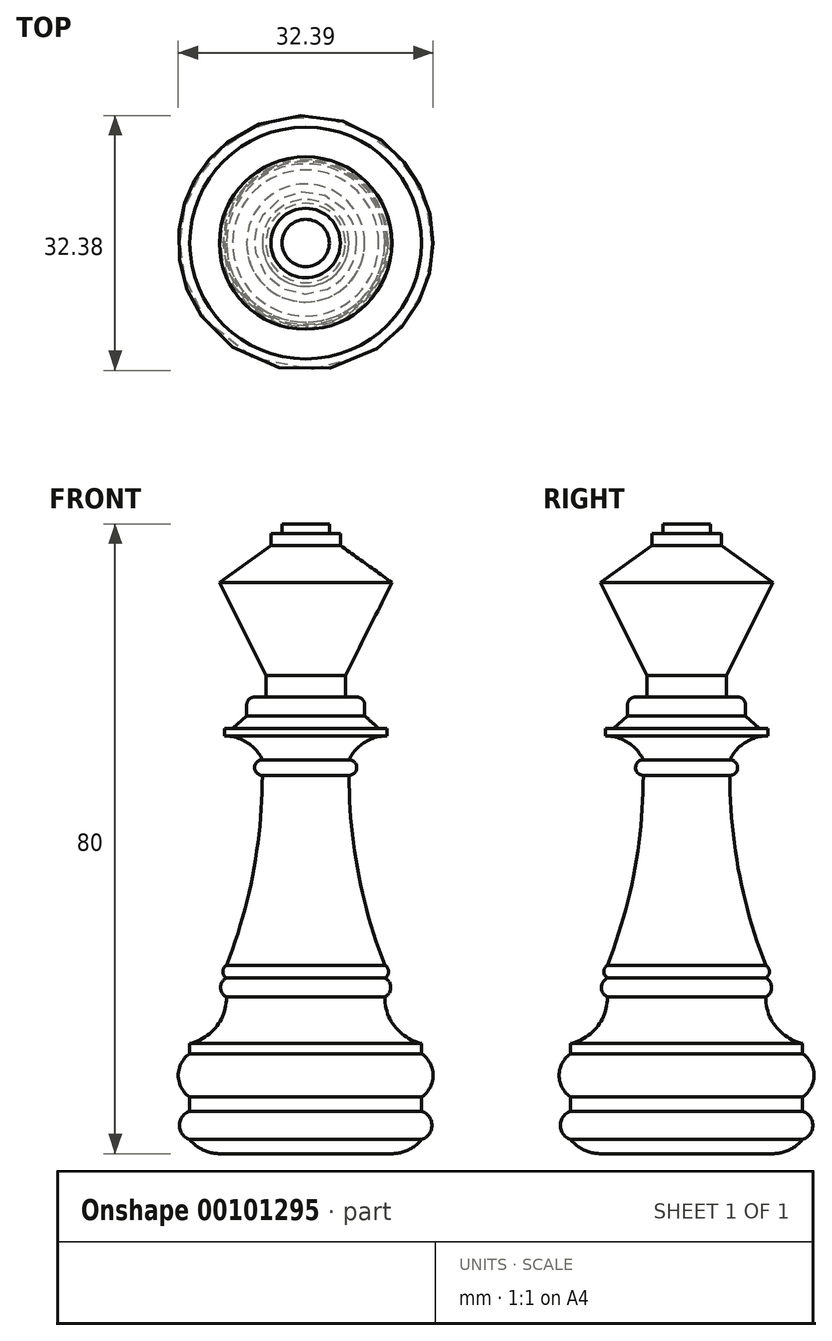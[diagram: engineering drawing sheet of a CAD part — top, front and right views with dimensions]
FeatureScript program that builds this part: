
annotation { "Feature Type Name" : "Feature", "Feature Type Description" : "" }
export const myFeature = defineFeature(function(context is Context, id is Id, definition is map)
    precondition{}
    {
        {
            var Q0;
            Q0=qCreatedBy(makeId("Front.planeOp"),FACE);
            var sketch = newSketch(context, id + "F0", { "sketchPlane" : qUnion([Q0])});
            skLineSegment(sketch, "E0", {"start": v(-203.37, 101.25) * mm, "end": v(-203.37, 21.25) * mm});
            skLineSegment(sketch, "E1", {"start": v(-203.37, 21.25) * mm, "end": v(-188.64, 21.25) * mm});
            skLineSegment(sketch, "E2", {"start": v(-188.64, 21.25) * mm, "end": v(-188.64, 23.04) * mm});
            skArc(sketch, "E3", {"start": v(-188.64, 23.04) * mm, "mid": v(-187.33, 24.85) * mm, "end": v(-188.64, 26.65) * mm});
            skLineSegment(sketch, "E4", {"start": v(-188.64, 26.65) * mm, "end": v(-188.64, 28.44) * mm});
            skArc(sketch, "E5", {"start": v(-188.64, 28.44) * mm, "mid": v(-187.17, 31.2) * mm, "end": v(-188.64, 33.94) * mm});
            skLineSegment(sketch, "E6", {"start": v(-188.64, 33.94) * mm, "end": v(-188.64, 35.24) * mm});
            skLineSegment(sketch, "E7", {"start": v(-188.64, 35.24) * mm, "end": v(-193.3, 35.24) * mm});
            skLineSegment(sketch, "E8", {"start": v(-193.3, 35.24) * mm, "end": v(-193.3, 41.17) * mm});
            skArc(sketch, "E9", {"start": v(-193.3, 41.17) * mm, "mid": v(-192.56, 42.37) * mm, "end": v(-193.3, 43.57) * mm});
            skArc(sketch, "E10", {"start": v(-193.3, 43.57) * mm, "mid": v(-192.84, 44.37) * mm, "end": v(-193.3, 45.17) * mm});
            skLineSegment(sketch, "E11", {"start": v(-197.86, 69.31) * mm, "end": v(-197.86, 45.17) * mm});
            skLineSegment(sketch, "E12", {"start": v(-197.86, 45.17) * mm, "end": v(-193.3, 45.17) * mm});
            skArc(sketch, "E13", {"start": v(-197.86, 69.31) * mm, "mid": v(-196.88, 70.3) * mm, "end": v(-197.86, 71.28) * mm});
            skLineSegment(sketch, "E14", {"start": v(-197.86, 71.28) * mm, "end": v(-197.86, 74.33) * mm});
            skLineSegment(sketch, "E15", {"start": v(-197.86, 74.33) * mm, "end": v(-193.04, 74.33) * mm});
            skLineSegment(sketch, "E16", {"start": v(-193.04, 74.33) * mm, "end": v(-193.04, 75.27) * mm});
            skLineSegment(sketch, "E17", {"start": v(-193.04, 75.27) * mm, "end": v(-194.08, 75.27) * mm});
            skLineSegment(sketch, "E18", {"start": v(-194.08, 75.27) * mm, "end": v(-195.87, 76.85) * mm});
            skLineSegment(sketch, "E19", {"start": v(-195.87, 76.85) * mm, "end": v(-195.87, 79.26) * mm});
            skLineSegment(sketch, "E20", {"start": v(-195.87, 79.26) * mm, "end": v(-198.32, 79.26) * mm});
            skArc(sketch, "E21", {"start": v(-198.32, 79.26) * mm, "mid": v(-197.8, 79.94) * mm, "end": v(-198.32, 80.62) * mm});
            skLineSegment(sketch, "E22", {"start": v(-198.32, 81.98) * mm, "end": v(-192.4, 93.8) * mm});
            skLineSegment(sketch, "E23", {"start": v(-192.4, 93.8) * mm, "end": v(-198.95, 98.5) * mm});
            skLineSegment(sketch, "E24", {"start": v(-198.95, 98.5) * mm, "end": v(-198.95, 100.03) * mm});
            skLineSegment(sketch, "E25", {"start": v(-198.95, 100.03) * mm, "end": v(-200.37, 100.03) * mm});
            skLineSegment(sketch, "E26", {"start": v(-200.37, 100.03) * mm, "end": v(-200.37, 101.25) * mm});
            skLineSegment(sketch, "E27", {"start": v(-200.37, 101.25) * mm, "end": v(-203.37, 101.25) * mm});
            skArc(sketch, "E28", {"start": v(-198.32, 80.62) * mm, "mid": v(-197.8, 81.3) * mm, "end": v(-198.32, 81.98) * mm});
            skLineSegment(sketch, "E29", {"start": v(-198.32, 81.98) * mm, "end": v(-198.32, 80.62) * mm});
            skLineSegment(sketch, "E30", {"start": v(-198.32, 79.26) * mm, "end": v(-198.32, 80.62) * mm});
            skSolve(sketch);
        }
        {
            var Q0;
            Q0=makeQuery(id+"F0.imprint","IMPRINT",FACE,{"disambiguationData":[TD([[makeQuery(id+"F0.imprint","IMPRINT",EDGE,{"derivedFrom":sQuery(id+"F0.wireOp",EDGE,"E0")}),1.0]])]});
            var Q1;
            Q1=sQuery(id+"F0.wireOp",EDGE,"E0");
            revolve(context, id + "F1", {"entities" : qUnion([Q0]), "axis" : qUnion([Q1]), "revolveType" : RevolveType.FULL});
        }
        {
            var Q0;
            Q0=makeQuery(id+"F1.opRevolve","SWEPT_EDGE",EDGE,{"disambiguationData":[OSD([sQuery(id+"F0.wireOp",EDGE,"E1"),sQuery(id+"F0.wireOp",EDGE,"E2")])]});
            fillet(context, id + "F2", {"entities" : qUnion([Q0]), "radius" : 5 * mm, "tangentPropagation" : true, "allowEdgeOverflow" : false});
        }
        {
            var Q0;
            Q0=makeQuery(id+"F1.opRevolve","SWEPT_EDGE",EDGE,{"disambiguationData":[OSD([sQuery(id+"F0.wireOp",EDGE,"E7"),sQuery(id+"F0.wireOp",EDGE,"E8")])]});
            var Q1;
            Q1=makeQuery(id+"F4.opFillet","BLEND_FACE",FACE,{"disambiguationData":[OSD([sQuery(id+"F0.wireOp",EDGE,"E11"),sQuery(id+"F0.wireOp",EDGE,"E12")])]});
            fillet(context, id + "F3", {"entities" : qUnion([Q0, Q1]), "radius" : 6 * mm, "tangentPropagation" : true, "allowEdgeOverflow" : false});
        }
        {
            var Q0;
            Q0=makeQuery(id+"F1.opRevolve","SWEPT_EDGE",EDGE,{"disambiguationData":[OSD([sQuery(id+"F0.wireOp",EDGE,"E11"),sQuery(id+"F0.wireOp",EDGE,"E12")])]});
            fillet(context, id + "F4", {"entities" : qUnion([Q0]), "radius" : 66.3 * mm, "tangentPropagation" : true, "allowEdgeOverflow" : false});
        }
        {
            var Q0;
            Q0=makeQuery(id+"F1.opRevolve","SWEPT_EDGE",EDGE,{"disambiguationData":[OSD([sQuery(id+"F0.wireOp",EDGE,"E14"),sQuery(id+"F0.wireOp",EDGE,"E15")])]});
            fillet(context, id + "F5", {"entities" : qUnion([Q0]), "radius" : 5.33 * mm, "tangentPropagation" : true, "allowEdgeOverflow" : false});
        }
        {
            var Q0;
            Q0=makeQuery(id+"F1.opRevolve","SWEPT_EDGE",EDGE,{"disambiguationData":[OSD([sQuery(id+"F0.wireOp",EDGE,"E19"),sQuery(id+"F0.wireOp",EDGE,"E20")])]});
            fillet(context, id + "F6", {"entities" : qUnion([Q0]), "radius" : 1 * mm, "tangentPropagation" : true, "allowEdgeOverflow" : false});
        }
    });
